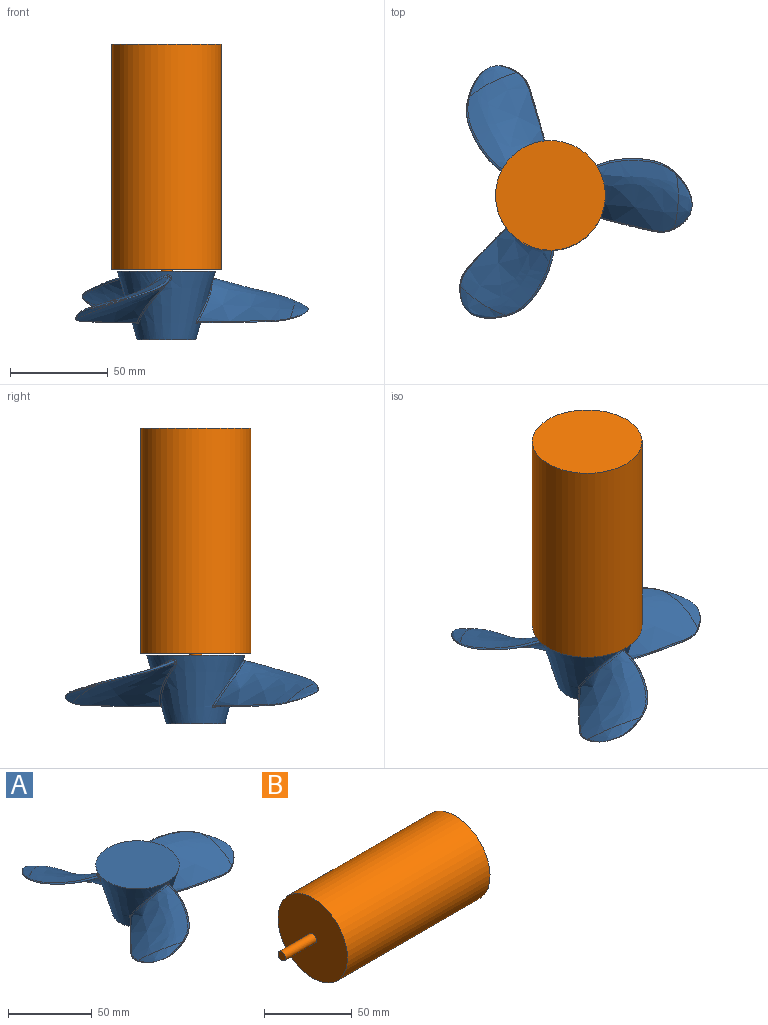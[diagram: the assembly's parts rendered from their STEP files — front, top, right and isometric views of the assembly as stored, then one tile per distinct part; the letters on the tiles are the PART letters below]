
ASSEMBLY  parts=2 mates=1
PART A: 39 faces, bbox 119.6x132.8x35 mm
  f0: bspline ~1.69x1.44mm, area 2.1mm2, adj f1,f3,f5,f36
  f1: bspline ~22.67x17.52mm, area 32.3mm2, adj f0,f2,f6,f36
  f2: bspline ~2.08x1.9mm, area 2.9mm2, adj f1,f3,f7,f36
  f3: bspline ~23.82x16.36mm, area 39.1mm2, adj f0,f2,f4,f36
  f4: bspline ~51.2x46.9mm, area 1622.9mm2, adj f3,f5,f7,f11
  f5: bspline ~36.95x31.21mm, area 60.3mm2, adj f0,f4,f6,f10
  f6: bspline ~50.98x47.9mm, area 1597.5mm2, adj f1,f5,f7,f9
  f7: bspline ~36.82x25.08mm, area 84.7mm2, adj f2,f4,f6,f8
  f8: bspline ~18.92x5.03mm, area 7.4mm2, adj f7,f9,f11
  f9: bspline ~23.44x17.71mm, area 104.3mm2, adj f6,f8,f10
  f10: bspline ~13.84x5.69mm, area 4.3mm2, adj f5,f9,f11
  f11: bspline ~23.35x17.72mm, area 108.4mm2, adj f4,f8,f10
  f12: bspline ~2.08x1.87mm, area 2.9mm2, adj f14,f15,f22,f36
  f13: bspline ~1.69x1.64mm, area 2.1mm2, adj f14,f15,f21,f36
  f14: bspline ~23.82x22.03mm, area 39.1mm2, adj f12,f13,f20,f36
  f15: bspline ~22.67x22.01mm, area 32.3mm2, adj f12,f13,f23,f36
  f16: bspline ~11.53x9.32mm, area 4mm2, adj f17,f19,f21
  f17: bspline ~27.13x9.77mm, area 108.4mm2, adj f16,f18,f20
  f18: bspline ~17.19x8.7mm, area 7.4mm2, adj f17,f19,f22
  f19: bspline ~27.18x9.75mm, area 104.3mm2, adj f16,f18,f23
  f20: bspline ~49.58x36.23mm, area 1622.9mm2, adj f14,f17,f21,f22
  f21: bspline ~47.28x10.54mm, area 60.3mm2, adj f13,f16,f20,f23
  f22: bspline ~44.32x12.5mm, area 84.7mm2, adj f12,f18,f20,f23
  f23: bspline ~50.52x37.77mm, area 1597.5mm2, adj f15,f19,f21,f22
  f24: bspline ~23.82x21.97mm, area 39.1mm2, adj f25,f27,f29,f36
  f25: bspline ~1.75x1.69mm, area 2.1mm2, adj f24,f26,f30,f36
  f26: bspline ~22.67x20.94mm, area 32.3mm2, adj f25,f27,f31,f36
  f27: bspline ~2.09x2.08mm, area 2.9mm2, adj f24,f26,f28,f36
  f28: bspline ~39.99x21.18mm, area 84.7mm2, adj f27,f29,f31,f35
  f29: bspline ~54.21x42.56mm, area 1622.9mm2, adj f24,f28,f30,f34
  f30: bspline ~45.09x16.71mm, area 60.3mm2, adj f25,f29,f31,f33
  f31: bspline ~55.32x42.25mm, area 1597.5mm2, adj f26,f28,f30,f32
  f32: bspline ~24.17x17.81mm, area 104.2mm2, adj f31,f33,f35
  f33: bspline ~14.65x5.45mm, area 4mm2, adj f30,f32,f34
  f34: bspline ~24.15x17.74mm, area 108.4mm2, adj f29,f33,f35
  f35: bspline ~15.58x10.85mm, area 7.4mm2, adj f28,f32,f34
  f36: cone r=15mm half-angle=15.9deg, axis (0,0,1), area 4075.9mm2, adj f0,f1,f2,f3,f12,f13,f14,f15
  f37: plane 30x30mm, normal (0,0,-1), area 706.9mm2, adj f36
  f38: plane 50x50mm, normal (0,0,1), area 1963.5mm2, adj f36
PART B: 5 faces, bbox 140x56x56 mm
  f0: plane 56x56mm, normal (1,0,0), area 2463mm2, adj f1
  f1: cylinder r=28mm len=115mm, axis (1,0,0), area 20231.9mm2, adj f0,f2
  f2: plane 56x56mm, normal (-1,0,0), area 2434.3mm2, adj f1,f3
  f3: cylinder r=3.02mm len=25mm, axis (1,0,0), area 474.7mm2, adj f2,f4
  f4: plane 6.04x6.04mm, normal (-1,0,0), area 28.7mm2, adj f3
PLACE A at identity
PLACE B rot(axis=(0,-1,0),90deg) t=(0,0,18.5)mm
MATE revolute B.f1 <-> A.f36  axis (0,0,1) through (0,0,76)mm
